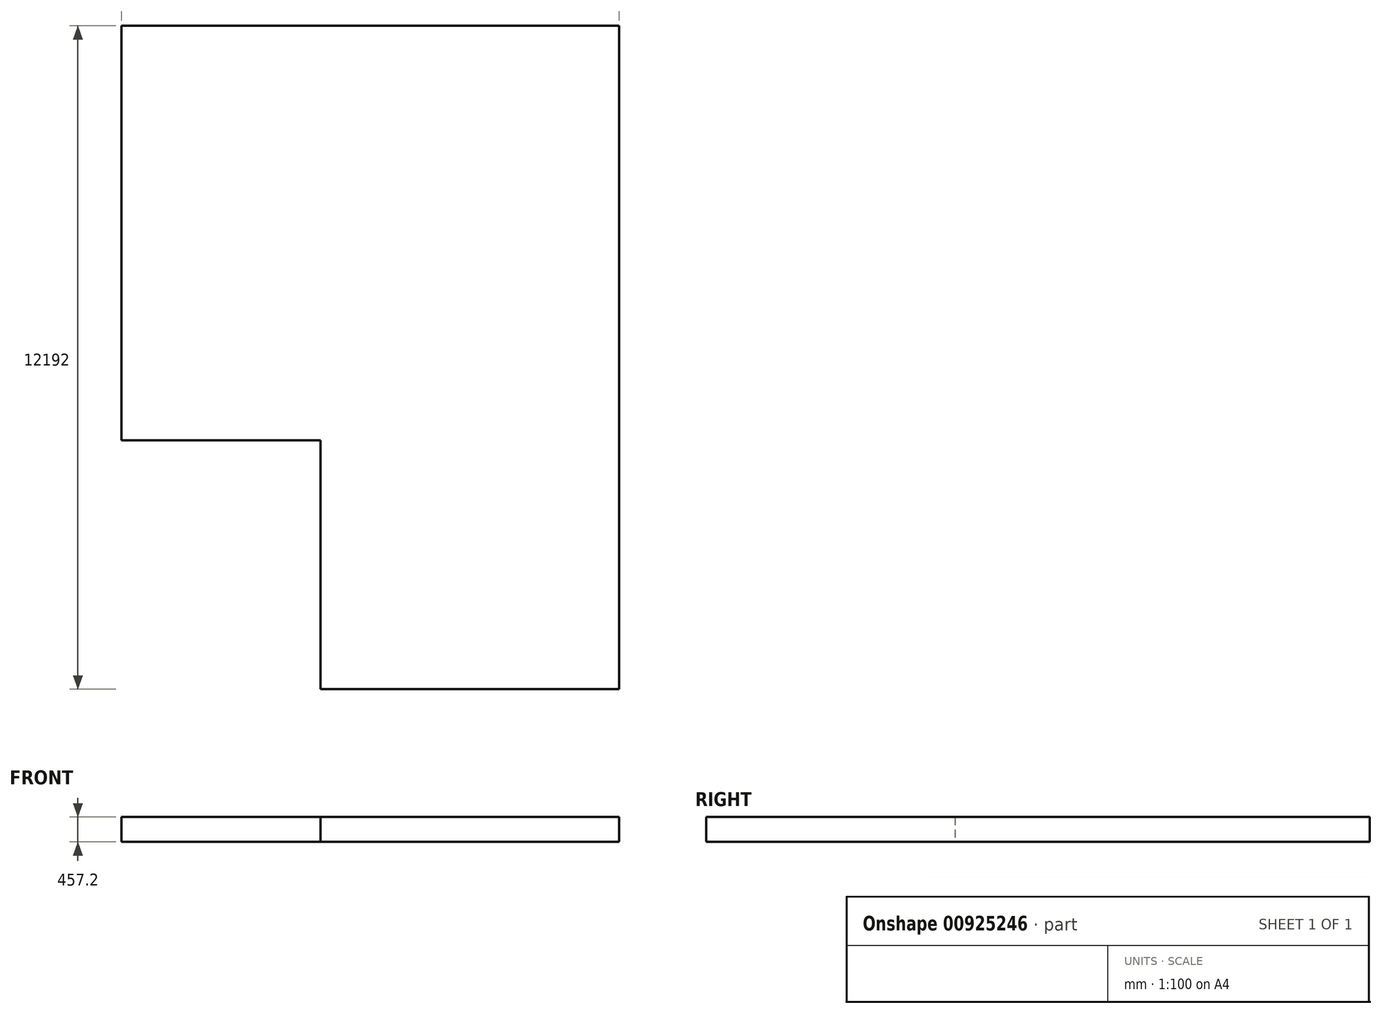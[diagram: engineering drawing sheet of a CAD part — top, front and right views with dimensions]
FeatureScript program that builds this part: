
annotation { "Feature Type Name" : "Feature", "Feature Type Description" : "" }
export const myFeature = defineFeature(function(context is Context, id is Id, definition is map)
    precondition{}
    {
        {
            var Q0;
            Q0=qCreatedBy(makeId("Top.planeOp"),FACE);
            var sketch = newSketch(context, id + "F0", { "sketchPlane" : qUnion([Q0])});
            skLineSegment(sketch, "E0.bottom", {"start": v(0, 0) * mm, "end": v(-5486.4, 0) * mm});
            skLineSegment(sketch, "E0.top", {"start": v(0, 12192) * mm, "end": v(-9144, 12192) * mm});
            skLineSegment(sketch, "E0.left", {"start": v(0, 0) * mm, "end": v(0, 12192) * mm});
            skLineSegment(sketch, "E0.right", {"start": v(-9144, 4572) * mm, "end": v(-9144, 12192) * mm});
            skLineSegment(sketch, "E1", {"start": v(-9144, 4572) * mm, "end": v(-5486.4, 4572) * mm});
            skLineSegment(sketch, "E2", {"start": v(-5486.4, 4572) * mm, "end": v(-5486.4, 0) * mm});
            skSolve(sketch);
        }
        {
            var Q0;
            Q0 = qSketchRegion(id + "F0", true);
            extrude(context, id + "F1", {"entities" : qUnion([Q0]), "depth" : 457.2 * mm, "offsetDistance" : 30.48 * mm});
        }
    });
